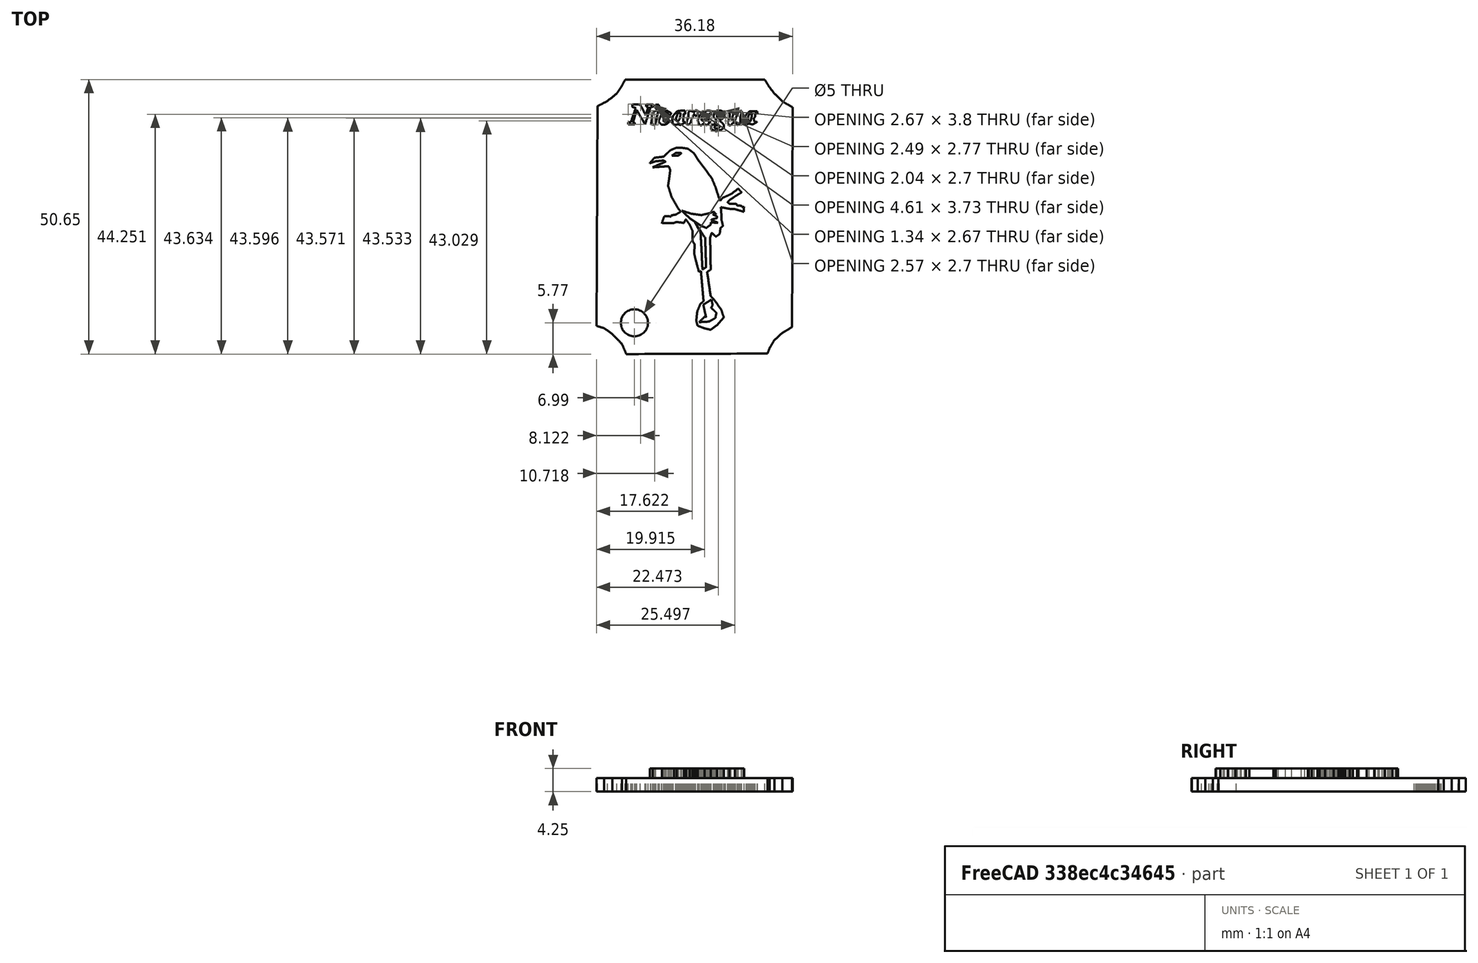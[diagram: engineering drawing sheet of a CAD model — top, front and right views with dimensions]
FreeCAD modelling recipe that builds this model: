
FCSTD DOCUMENT  (FreeCAD 0.16R)
Label: llavero_gurdabaranco
License: All rights reserved
LicenseURL: http://en.wikipedia.org/wiki/All_rights_reserved
objects: Part::Feature×22, Part::MultiFuse×3, Part::Extrusion×3, Part::Cut×2, Part::Cylinder×1
note: 31 computed .brp shape members not serialized (recipe doc carries the construction recipe); baked Part::Feature solids carry a one-line shape summary decoded from their .brp

FEATURE [Part::Feature] path3596  label="Marco"
  shape: bbox 36.18 x 50.65 x 2e-07 mm, 0 faces, 0 solids (baked)
FEATURE [Part::Feature] path3598
  shape: bbox 17.39 x 33.61 x 2e-07 mm, 0 faces, 0 solids (baked)
FEATURE [Part::Feature] path3600
  shape: bbox 6.652 x 3.175 x 2e-07 mm, 0 faces, 0 solids (baked)
FEATURE [Part::Feature] path3602
  shape: bbox 2.016 x 8.618 x 2e-07 mm, 0 faces, 0 solids (baked)
FEATURE [Part::Feature] path3604
  shape: bbox 3.175 x 4.183 x 2e-07 mm, 0 faces, 0 solids (baked)
FEATURE [Part::Feature] path3606
  shape: bbox 1.764 x 0.5544 x 2e-07 mm, 0 faces, 0 solids (baked)
FEATURE [Part::Feature] path3608
  shape: bbox 4.611 x 3.729 x 2e-07 mm, 0 faces, 0 solids (baked)
FEATURE [Part::Feature] path3610
  shape: bbox 1.336 x 2.671 x 2e-07 mm, 0 faces, 0 solids (baked)
FEATURE [Part::Feature] path3612
  shape: bbox 2.318 x 2.621 x 2e-07 mm, 0 faces, 0 solids (baked)
FEATURE [Part::Feature] path3614
  shape: bbox 0.9323 x 0.63 x 2e-07 mm, 0 faces, 0 solids (baked)
FEATURE [Part::Feature] path3616
  shape: bbox 2.419 x 2.671 x 2e-07 mm, 0 faces, 0 solids (baked)
FEATURE [Part::Feature] path3618
  shape: bbox 0.8819 x 1.512 x 2e-07 mm, 0 faces, 0 solids (baked)
FEATURE [Part::Feature] path3620
  shape: bbox 2.041 x 2.696 x 2e-07 mm, 0 faces, 0 solids (baked)
FEATURE [Part::Feature] path3622
  shape: bbox 2.495 x 2.772 x 2e-07 mm, 0 faces, 0 solids (baked)
FEATURE [Part::Feature] path3624
  shape: bbox 0.882 x 1.537 x 2e-07 mm, 0 faces, 0 solids (baked)
FEATURE [Part::Feature] path3626
  shape: bbox 2.671 x 3.805 x 2e-07 mm, 0 faces, 0 solids (baked)
FEATURE [Part::Feature] path3628
  shape: bbox 0.8316 x 1.109 x 2e-07 mm, 0 faces, 0 solids (baked)
FEATURE [Part::Feature] path3630
  shape: bbox 1.033 x 0.5796 x 2e-07 mm, 0 faces, 0 solids (baked)
FEATURE [Part::Feature] path3632
  shape: bbox 2.57 x 2.696 x 2e-07 mm, 0 faces, 0 solids (baked)
FEATURE [Part::Feature] path3634
  shape: bbox 2.495 x 2.444 x 2e-07 mm, 0 faces, 0 solids (baked)
FEATURE [Part::Feature] path3636
  shape: bbox 0.756 x 1.512 x 2e-07 mm, 0 faces, 0 solids (baked)
FEATURE [Part::MultiFuse] Fusion  label="Guardabaranco"
  Shapes = -> [path3598,path3600,path3602,path3604,path3606]
FEATURE [Part::MultiFuse] Fusion001  label="Nicaragua"
  Shapes = -> [path3608,path3610,path3612,path3614,path3616,path3618,path3620,path3622,path3624,path3626,path3628,path3630,path3632,path3634,path3636]
FEATURE [Part::Extrusion] Extrude
  Base = -> path3596
  Dir = (0,0,2.5)
  Solid = true
FEATURE [Part::Extrusion] Extrude001
  Base = -> Fusion
  Dir = (0,0,4)
  Placement = pos=(0,0,0.25) rot=(0,0,1;0rad)
  Solid = true
FEATURE [Part::Extrusion] Extrude002
  Base = -> Fusion001
  Dir = (0,0,4)
  Solid = true
FEATURE [Part::Cut] Cut
  Base = -> Extrude
  Tool = -> Extrude002
FEATURE [Part::Cylinder] Cylinder
  Angle = 360
  Height = 10
  Placement = pos=(-24,5,-3) rot=(0,0,1;0rad)
  Radius = 2.5
FEATURE [Part::Cut] Cut001
  Base = -> Cut
  Tool = -> Cylinder
FEATURE [Part::MultiFuse] Fusion002  label="llavero"
  Shapes = -> [Extrude001,Cut001]
FEATURE [Part::Feature] Fusion002001  label="Lavero terminado"
  shape: bbox 36.18 x 50.65 x 4.25 mm, 347 faces, 6 solids (baked)
